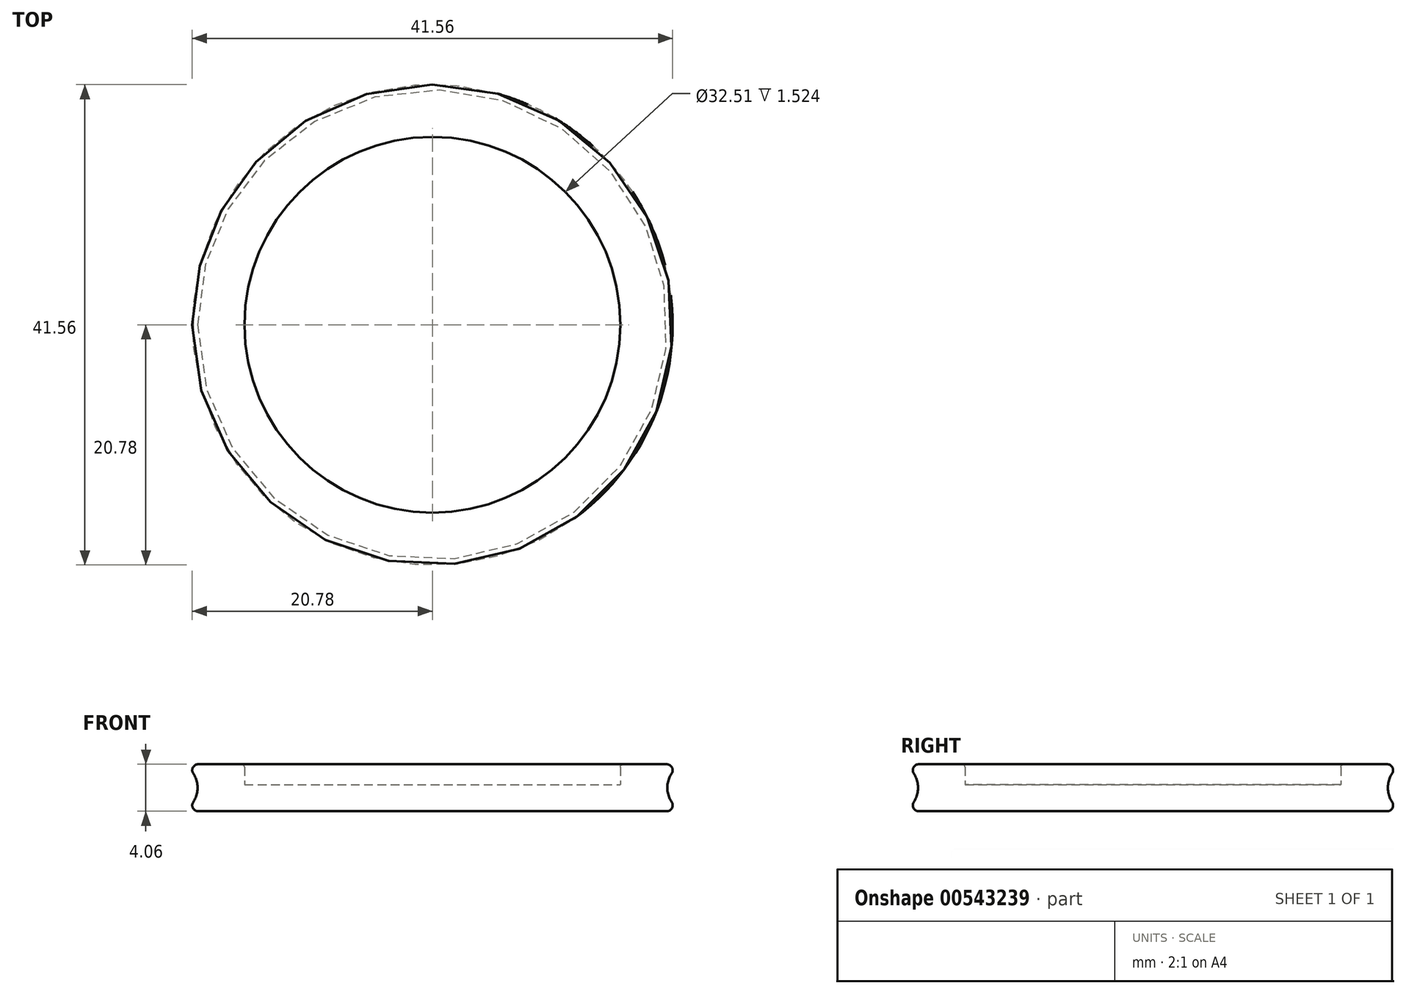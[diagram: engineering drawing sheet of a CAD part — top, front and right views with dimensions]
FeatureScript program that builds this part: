
annotation { "Feature Type Name" : "Feature", "Feature Type Description" : "" }
export const myFeature = defineFeature(function(context is Context, id is Id, definition is map)
    precondition{}
    {
        {
            var Q0;
            Q0=qCreatedBy(makeId("Front.planeOp"),FACE);
            var sketch = newSketch(context, id + "F0", { "sketchPlane" : qUnion([Q0])});
            skLineSegment(sketch, "E0", {"start": v(0, 0) * mm, "end": v(0, 2.29) * mm});
            skLineSegment(sketch, "E1", {"start": v(0, 2.29) * mm, "end": v(-16.26, 2.29) * mm});
            skLineSegment(sketch, "E2", {"start": v(-16.26, 2.29) * mm, "end": v(-16.26, 4.06) * mm});
            skLineSegment(sketch, "E3", {"start": v(-16.26, 4.06) * mm, "end": v(-21.6, 4.06) * mm});
            skLineSegment(sketch, "E4", {"start": v(-21.59, 0) * mm, "end": v(0, 0) * mm});
            skArc(sketch, "E5", {"start": v(-21.6, 0) * mm, "mid": v(-20.32, 2.03) * mm, "end": v(-21.6, 4.06) * mm});
            skLineSegment(sketch, "E6", {"start": v(-21.6, 4.06) * mm, "end": v(-21.6, 0) * mm, "construction": true});
            skLineSegment(sketch, "E7", {"start": v(-20.32, 2.03) * mm, "end": v(-20.32, 6.77) * mm, "construction": true});
            skSolve(sketch);
        }
        {
            var Q0;
            Q0 = qSketchRegion(id + "F0", true);
            var Q1;
            Q1=sQuery(id+"F0.wireOp",EDGE,"E0");
            revolve(context, id + "F1", {"entities" : qUnion([Q0]), "axis" : qUnion([Q1]), "revolveType" : RevolveType.FULL});
        }
        {
            var Q0;
            Q0=makeQuery(id+"F1.opRevolve","SWEPT_EDGE",EDGE,{"disambiguationData":[OSD([sQuery(id+"F0.wireOp",EDGE,"E3"),sQuery(id+"F0.wireOp",EDGE,"E5")])]});
            var Q1;
            Q1=makeQuery(id+"F1.opRevolve","SWEPT_EDGE",EDGE,{"disambiguationData":[OSD([sQuery(id+"F0.wireOp",EDGE,"E4"),sQuery(id+"F0.wireOp",EDGE,"E5")])]});
            fillet(context, id + "F2", {"entities" : qUnion([Q0, Q1]), "radius" : 0.5 * mm, "tangentPropagation" : true, "allowEdgeOverflow" : false});
        }
        {
            var Q0;
            Q0=makeQuery(id+"F1.opRevolve","SWEPT_EDGE",EDGE,{"disambiguationData":[OSD([sQuery(id+"F0.wireOp",EDGE,"E2"),sQuery(id+"F0.wireOp",EDGE,"E3")])]});
            fillet(context, id + "F3", {"entities" : qUnion([Q0]), "radius" : 0.25 * mm, "tangentPropagation" : true, "allowEdgeOverflow" : false});
        }
    });
